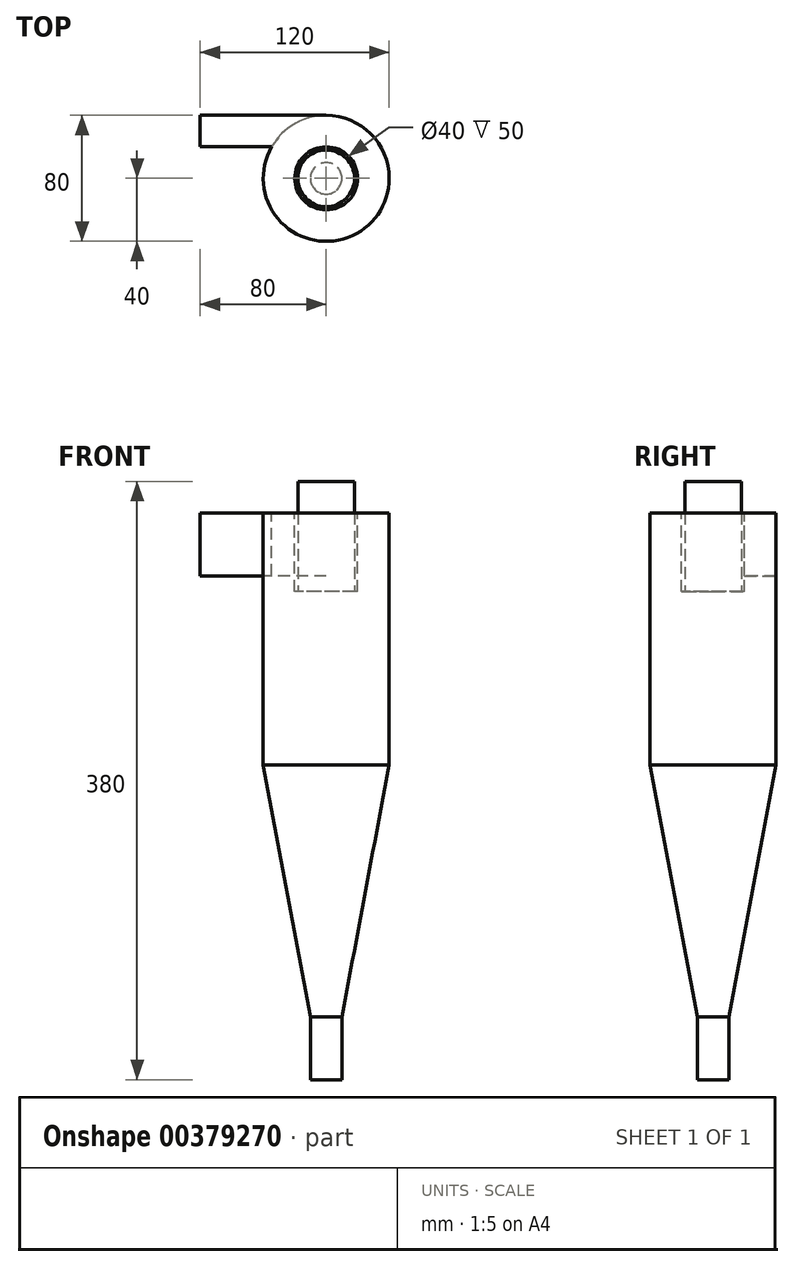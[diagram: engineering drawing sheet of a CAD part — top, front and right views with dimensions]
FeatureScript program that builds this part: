
annotation { "Feature Type Name" : "Feature", "Feature Type Description" : "" }
export const myFeature = defineFeature(function(context is Context, id is Id, definition is map)
    precondition{}
    {
        {
            var Q0;
            Q0=qCreatedBy(makeId("Top.planeOp"),FACE);
            var sketch = newSketch(context, id + "F0", { "sketchPlane" : qUnion([Q0])});
            skCircle(sketch, "E0", {"center": v(0, 0) * mm, "radius": 40 * mm});
            skSolve(sketch);
        }
        {
            var Q0;
            Q0 = qSketchRegion(id + "F0", true);
            extrude(context, id + "F1", {"entities" : qUnion([Q0]), "oppositeDirection" : true, "depth" : 160 * mm});
        }
        {
            var Q0;
            Q0=makeQuery(id+"F1.opExtrude","CAP_FACE",FACE,{"disambiguationData":[OSD([sQuery(id+"F0.wireOp",EDGE,"E0")])],"isStart":false});
            cPlane(context, id + "F2", {"entities" : qUnion([Q0]), "cplaneType" : CPlaneType.OFFSET, "offset" : 160 * mm, "width" : 150 * mm, "height" : 150 * mm});
        }
        {
            var Q0;
            Q0=qCreatedBy(id+"F2.planeOp",FACE);
            var sketch = newSketch(context, id + "F3", { "sketchPlane" : qUnion([Q0])});
            skCircle(sketch, "E1", {"center": v(0, 0) * mm, "radius": 10 * mm});
            skSolve(sketch);
        }
        {
            var Q1;
            Q1=makeQuery(id+"F3.imprint","IMPRINT",FACE,{"disambiguationData":[TD([[makeQuery(id+"F3.imprint","IMPRINT",EDGE,{"derivedFrom":sQuery(id+"F3.wireOp",EDGE,"E1")}),1.0]])]});
            var Q2;
            Q2=makeQuery(id+"F1.opExtrude","CAP_FACE",FACE,{"disambiguationData":[OSD([sQuery(id+"F0.wireOp",EDGE,"E0")])],"isStart":false});
            loft(context, id + "F4", {"operationType" : NewBodyOperationType.ADD, "sheetProfilesArray" : [{ "sheetProfileEntities" : qUnion([Q1]) }, { "sheetProfileEntities" : qUnion([Q2]) }]});
        }
        {
            var Q0;
            Q0=makeQuery(id+"F4.opLoft","CAP_FACE",FACE,{"disambiguationData":[OSD([makeQuery(id+"F3.imprint","IMPRINT",FACE,{"disambiguationData":[TD([[makeQuery(id+"F3.imprint","IMPRINT",EDGE,{"derivedFrom":sQuery(id+"F3.wireOp",EDGE,"E1")}),1.0]])]})])],"isStart":true});
            extrude(context, id + "F5", {"entities" : qUnion([Q0]), "operationType" : NewBodyOperationType.ADD, "depth" : 40 * mm});
        }
        {
            var Q0;
            Q0=qCreatedBy(makeId("Top.planeOp"),FACE);
            var sketch = newSketch(context, id + "F6", { "sketchPlane" : qUnion([Q0])});
            skLineSegment(sketch, "E2.bottom", {"start": v(0, 20) * mm, "end": v(-80, 20) * mm});
            skLineSegment(sketch, "E2.top", {"start": v(0, 40) * mm, "end": v(-80, 40) * mm});
            skLineSegment(sketch, "E2.left", {"start": v(0, 20) * mm, "end": v(0, 40) * mm});
            skLineSegment(sketch, "E2.right", {"start": v(-80, 20) * mm, "end": v(-80, 40) * mm});
            skSolve(sketch);
        }
        {
            var Q0;
            Q0=makeQuery(id+"F6.imprint","IMPRINT",FACE,{"disambiguationData":[TD([[makeQuery(id+"F6.imprint","IMPRINT",EDGE,{"derivedFrom":sQuery(id+"F6.wireOp",EDGE,"E2.bottom")}),-1.0]])]});
            extrude(context, id + "F7", {"entities" : qUnion([Q0]), "operationType" : NewBodyOperationType.ADD, "oppositeDirection" : true, "depth" : 40 * mm});
        }
        {
            var Q0;
            Q0=makeQuery(id+"F7.boolean.opBoolean","MERGE",FACE,{"derivedFrom":[makeQuery(id+"F1.opExtrude","CAP_FACE",FACE,{"disambiguationData":[OSD([sQuery(id+"F0.wireOp",EDGE,"E0")])],"isStart":true}),makeQuery(id+"F7.opExtrude","CAP_FACE",FACE,{"disambiguationData":[OSD([sQuery(id+"F6.wireOp",EDGE,"E2.bottom"),sQuery(id+"F6.wireOp",EDGE,"E2.top"),sQuery(id+"F6.wireOp",EDGE,"E2.left"),sQuery(id+"F6.wireOp",EDGE,"E2.right")])],"isStart":true})]});
            var sketch = newSketch(context, id + "F8", { "sketchPlane" : qUnion([Q0])});
            skCircle(sketch, "E3", {"center": v(0, 0) * mm, "radius": 18 * mm});
            skSolve(sketch);
        }
        {
            var Q0;
            Q0=makeQuery(id+"F8.imprint","IMPRINT",FACE,{"disambiguationData":[TD([[makeQuery(id+"F8.imprint","IMPRINT",EDGE,{"derivedFrom":sQuery(id+"F8.wireOp",EDGE,"E3")}),1.0]])]});
            extrude(context, id + "F9", {"entities" : qUnion([Q0]), "operationType" : NewBodyOperationType.ADD, "depth" : 20 * mm});
        }
        {
            var Q0;
            Q0=makeQuery(id+"F7.boolean.opBoolean","MERGE",FACE,{"derivedFrom":[makeQuery(id+"F1.opExtrude","CAP_FACE",FACE,{"disambiguationData":[OSD([sQuery(id+"F0.wireOp",EDGE,"E0")])],"isStart":true}),makeQuery(id+"F7.opExtrude","CAP_FACE",FACE,{"disambiguationData":[OSD([sQuery(id+"F6.wireOp",EDGE,"E2.bottom"),sQuery(id+"F6.wireOp",EDGE,"E2.top"),sQuery(id+"F6.wireOp",EDGE,"E2.left"),sQuery(id+"F6.wireOp",EDGE,"E2.right")])],"isStart":true})]});
            var sketch = newSketch(context, id + "F10", { "sketchPlane" : qUnion([Q0])});
            skCircle(sketch, "E4", {"center": v(0, 0) * mm, "radius": 20 * mm});
            skSolve(sketch);
        }
        {
            var Q0;
            Q0=makeQuery(id+"F10.imprint","IMPRINT",FACE,{"disambiguationData":[TD([[makeQuery(id+"F10.imprint","IMPRINT",EDGE,{"derivedFrom":sQuery(id+"F10.wireOp",EDGE,"E4")}),1.0]])]});
            extrude(context, id + "F11", {"entities" : qUnion([Q0]), "operationType" : NewBodyOperationType.REMOVE, "oppositeDirection" : true, "depth" : 50 * mm});
        }
    });
